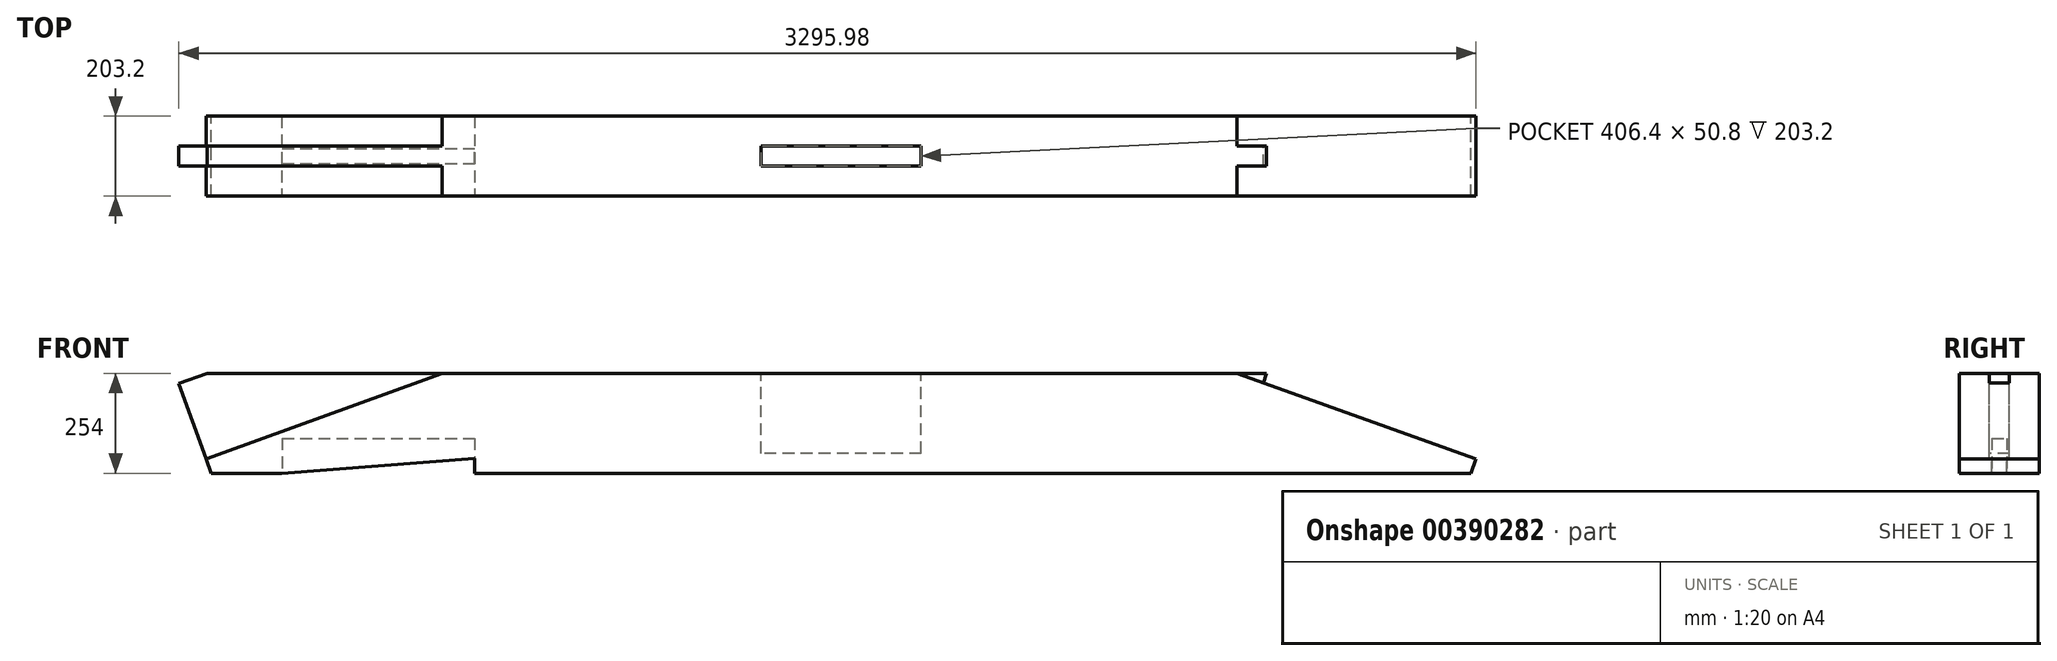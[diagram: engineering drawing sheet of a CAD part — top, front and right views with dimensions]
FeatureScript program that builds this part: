
annotation { "Feature Type Name" : "Feature", "Feature Type Description" : "" }
export const myFeature = defineFeature(function(context is Context, id is Id, definition is map)
    precondition{}
    {
        {
            var Q0;
            Q0=qCreatedBy(makeId("Front.planeOp"),FACE);
            var sketch = newSketch(context, id + "F0", { "sketchPlane" : qUnion([Q0])});
            skLineSegment(sketch, "E0.bottom", {"start": v(-1714.5, 127) * mm, "end": v(1714.5, 127) * mm});
            skLineSegment(sketch, "E0.top", {"start": v(-1714.5, -127) * mm, "end": v(1714.5, -127) * mm});
            skLineSegment(sketch, "E0.left", {"start": v(-1714.5, 127) * mm, "end": v(-1714.5, -127) * mm});
            skLineSegment(sketch, "E0.right", {"start": v(1714.5, 127) * mm, "end": v(1714.5, -127) * mm});
            skPoint(sketch, "E0.middle", {"position": v(0, 0) * mm});
            skLineSegment(sketch, "E1", {"start": v(-1714.5, -127) * mm, "end": v(-1014.27, 127) * mm});
            skLineSegment(sketch, "E2", {"start": v(1714.5, -127) * mm, "end": v(1005.59, 127) * mm});
            skLineSegment(sketch, "E3", {"start": v(1613.2, -90.7) * mm, "end": v(1072.32, 103.09) * mm});
            skLineSegment(sketch, "E4", {"start": v(1600.2, -127) * mm, "end": v(1681.74, 100.59) * mm});
            skLineSegment(sketch, "E5", {"start": v(1681.74, 100.59) * mm, "end": v(1608.02, 127) * mm});
            skLineSegment(sketch, "E6", {"start": v(1608.02, 127) * mm, "end": v(1080.9, 127) * mm});
            skLineSegment(sketch, "E7", {"start": v(1080.9, 127) * mm, "end": v(1072.32, 103.09) * mm});
            skLineSegment(sketch, "E8", {"start": v(-1600.2, -127) * mm, "end": v(-1682.78, 100.66) * mm});
            skLineSegment(sketch, "E9", {"start": v(-1682.78, 100.66) * mm, "end": v(-1610.17, 127) * mm});
            skLineSegment(sketch, "E10", {"start": v(-1610.17, 127) * mm, "end": v(-1088.76, 127) * mm});
            skLineSegment(sketch, "E11", {"start": v(-1088.76, 127) * mm, "end": v(-1080.1, 103.12) * mm});
            skSolve(sketch);
        }
        {
            var Q0;
            {var subQ0=sQuery(id+"F0.wireOp",EDGE,"E1");var subQ1=sQuery(id+"F0.wireOp",EDGE,"E0.bottom");var subQ2=makeQuery(id+"F0.imprint","INTERSECT",VERTEX,{"derivedFrom":[subQ1,subQ0]});Q0=makeQuery(id+"F0.imprint","IMPRINT",FACE,{"disambiguationData":[TD([[makeQuery(id+"F0.imprint","IMPRINT",EDGE,{"disambiguationData":[TD([[subQ2,-1.0]])],"derivedFrom":subQ1}),-1.0]])]});}
            extrude(context, id + "F1", {"entities" : qUnion([Q0]), "endBound" : BoundingType.SYMMETRIC, "depth" : 203.2 * mm});
        }
        {
            var Q0;
            {var subQ0=sQuery(id+"F0.wireOp",EDGE,"C5tzmZHX-IM7C-lst4-VYUM-Vyus2H2f5oGW");Q0=makeQuery(id+"F0.imprint","IMPRINT",FACE,{"disambiguationData":[TD([[makeQuery(id+"F0.imprint","IMPRINT",EDGE,{"derivedFrom":subQ0}),-1.0]])]});}
            var Q1;
            {var subQ0=sQuery(id+"F0.wireOp",EDGE,"E9");Q1=makeQuery(id+"F0.imprint","IMPRINT",FACE,{"disambiguationData":[TD([[makeQuery(id+"F0.imprint","IMPRINT",EDGE,{"derivedFrom":subQ0}),-1.0]])]});}
            var Q2;
            {var subQ2=sQuery(id+"F0.wireOp",EDGE,"E3");Q2=makeQuery(id+"F0.imprint","IMPRINT",FACE,{"disambiguationData":[TD([[makeQuery(id+"F0.imprint","IMPRINT",EDGE,{"derivedFrom":subQ2}),-1.0]])]});}
            var Q3;
            {var subQ3=sQuery(id+"F0.wireOp",EDGE,"E7");Q3=makeQuery(id+"F0.imprint","IMPRINT",FACE,{"disambiguationData":[TD([[makeQuery(id+"F0.imprint","IMPRINT",EDGE,{"derivedFrom":subQ3}),-1.0]])]});}
            var Q4;
            {var subQ3=sQuery(id+"F0.wireOp",EDGE,"E11");Q4=makeQuery(id+"F0.imprint","IMPRINT",FACE,{"disambiguationData":[TD([[makeQuery(id+"F0.imprint","IMPRINT",EDGE,{"derivedFrom":subQ3}),1.0]])]});}
            extrude(context, id + "F2", {"entities" : qUnion([Q0, Q1, Q2, Q3, Q4]), "operationType" : NewBodyOperationType.ADD, "endBound" : BoundingType.SYMMETRIC, "depth" : 50.8 * mm});
        }
        {
            var Q0;
            Q0=makeQuery(id+"F1.opExtrude","SWEPT_FACE",FACE,{"disambiguationData":[OSD([sQuery(id+"F0.wireOp",EDGE,"E0.bottom")])]});
            var sketch = newSketch(context, id + "F3", { "sketchPlane" : qUnion([Q0])});
            skLineSegment(sketch, "E12.bottom", {"start": v(203.2, 25.4) * mm, "end": v(-203.2, 25.4) * mm});
            skLineSegment(sketch, "E12.top", {"start": v(203.2, -25.4) * mm, "end": v(-203.2, -25.4) * mm});
            skLineSegment(sketch, "E12.left", {"start": v(203.2, 25.4) * mm, "end": v(203.2, -25.4) * mm});
            skLineSegment(sketch, "E12.right", {"start": v(-203.2, 25.4) * mm, "end": v(-203.2, -25.4) * mm});
            skPoint(sketch, "E12.middle", {"position": v(0, 0) * mm});
            skSolve(sketch);
        }
        {
            var Q0;
            Q0 = qSketchRegion(id + "F3", true);
            extrude(context, id + "F4", {"entities" : qUnion([Q0]), "operationType" : NewBodyOperationType.REMOVE, "oppositeDirection" : true, "depth" : 203.2 * mm});
        }
        {
            var Q0;
            Q0=makeQuery(id+"F1.opExtrude","SWEPT_FACE",FACE,{"disambiguationData":[OSD([sQuery(id+"F0.wireOp",EDGE,"E0.top")])]});
            var sketch = newSketch(context, id + "F5", { "sketchPlane" : qUnion([Q0])});
            skLineSegment(sketch, "E13.bottom", {"start": v(-1419.8, 19.05) * mm, "end": v(-931.34, 19.05) * mm});
            skLineSegment(sketch, "E13.top", {"start": v(-1419.8, -19.05) * mm, "end": v(-931.34, -19.05) * mm});
            skLineSegment(sketch, "E13.left", {"start": v(-1419.8, 19.05) * mm, "end": v(-1419.8, -19.05) * mm});
            skLineSegment(sketch, "E13.right", {"start": v(-931.34, 19.05) * mm, "end": v(-931.34, -19.05) * mm});
            skPoint(sketch, "E13.middle", {"position": v(-1175.58, 0) * mm});
            skSolve(sketch);
        }
        {
            var Q0;
            Q0=makeQuery(id+"F5.imprint","IMPRINT",FACE,{"disambiguationData":[TD([[makeQuery(id+"F5.imprint","IMPRINT",EDGE,{"derivedFrom":sQuery(id+"F5.wireOp",EDGE,"E13.bottom")}),-1.0]])]});
            extrude(context, id + "F6", {"entities" : qUnion([Q0]), "operationType" : NewBodyOperationType.REMOVE, "oppositeDirection" : true, "depth" : 88.9 * mm});
        }
        {
            var Q0;
            Q0=makeQuery(id+"F1.opExtrude","CAP_FACE",FACE,{"disambiguationData":[OSD([sQuery(id+"F0.wireOp",EDGE,"E0.bottom"),sQuery(id+"F0.wireOp",EDGE,"E0.top"),sQuery(id+"F0.wireOp",EDGE,"E1"),sQuery(id+"F0.wireOp",EDGE,"E2"),sQuery(id+"F0.wireOp",EDGE,"E3"),sQuery(id+"F0.wireOp",EDGE,"E4"),sQuery(id+"F0.wireOp",EDGE,"E8")])],"isStart":false});
            var sketch = newSketch(context, id + "F7", { "sketchPlane" : qUnion([Q0])});
            skLineSegment(sketch, "E14", {"start": v(-931.27, -127) * mm, "end": v(-931.27, -88.9) * mm});
            skLineSegment(sketch, "E15", {"start": v(-931.27, -88.9) * mm, "end": v(-1421.5, -127) * mm});
            skSolve(sketch);
        }
        {
            var Q0;
            {var subQ0=sQuery(id+"F7.wireOp",EDGE,"E14");Q0=makeQuery(id+"F7.imprint","IMPRINT",FACE,{"disambiguationData":[TD([[makeQuery(id+"F7.imprint","IMPRINT",EDGE,{"derivedFrom":subQ0}),1.0]])]});}
            extrude(context, id + "F8", {"entities" : qUnion([Q0]), "operationType" : NewBodyOperationType.REMOVE, "oppositeDirection" : true, "depth" : 203.2 * mm});
        }
    });
